# Revit family: MAXXflo EVO CWH 150-302
name_source: partatom
category: Generic Models
units: mm (PartAtom-declared; Revit-internal decimal feet)

## family parameters
Always vertical = Yes
Can host rebar = No
Cut with Voids When Loaded = No
Part Type = Normal
Room Calculation Point = No
Round Connector Dimension = Use Diameter
Shared = No
Work Plane-Based = No

## types (1)
- Standard
    6 Monthly = 0
    Access Clearance Bottom = 0 mm  [stored 0 ft]
    Access Clearance Front = 800 mm  [stored 2.62467 ft]
    Access Clearance Left = 300 mm
    Access Clearance Rear = 20 mm  [stored 0.0656168 ft]
    Access Clearance Right = 25 mm  [stored 0.082021 ft]
    Access Clearance Top = 400 mm  [stored 1.31234 ft]
    Air Inlet Connection Size = 200 mm  [stored 0.656168 ft]
    Annually = 32-12, 32.13, 32-10,
    BMS Links = Yes
    Bespoke Timeframe = 0
    CE Approval = 0558DL2312
    Clean Out Cover and Inspection Opening Size = 0 mm  [stored 0 ft]
    Colour = Cover = White (RAL 9016), Tower = Anthracite Grey (RAL 7016), Base = Dark Grey (RAL 7021)
    Condensate Drain Connection Type = Other
    Condensate Drain Size = 41 mm  [stored 0.134514 ft]
    Connector_1_Diameter = 45 mm
    Connector_2_Diameter = 30 mm  [stored 0.0984252 ft]
    Connector_3_Diameter = 45 mm
    Connector_4_Diameter = 30 mm  [stored 0.0984252 ft]
    Connector_5_Diameter = 28 mm  [stored 0.0918635 ft]
    Connector_6_Diameter = 28 mm  [stored 0.0918635 ft]
    Connector_7_Diameter = 41 mm  [stored 0.134514 ft]
    Connector_8_Diameter = 200 mm  [stored 0.656168 ft]
    Continuous output at 44 degree differential = 0.81000 L/s
    Continuous output at 50 degree differential = 0.71000 L/s
    Control Options = On/off
    Control Thermostat Range = 5-65ºC
    Control Type = Internal
    Daily = 0
    Default Elevation = 0 mm  [stored 0 ft]
    Description = BIM Model MAXXflo EVO CWH150/302
    Drain Connection Size = 22 mm  [stored 0.0721785 ft]
    Drain Connection Type = Other
    Embodied Carbon = 0
    Energy Technology List = 0
    Environmental Product Declaration = 0
    ErP Energy Label = A
    Expected Life = 10
    External Material = Steel
    Features = High efficiency condensing stainless steel; direct storage water heater
    Finish = Painted
    Flow and Return Connection Size = 38 mm
    Flow and Return Connection Type = Threaded
    Flue Connection size = 130 mm  [stored 0.426509 ft]
    Flue or Air Intake Classification = B23, C13, C33 C53, C63
    Frequency = 50 Hz
    Fuel Connection Size = 25 mm  [stored 0.082021 ft]
    Fuel Connection Type = Threaded
    Fuel Type = Gas - NG
    Full Load Current = 1.560 A
    Fuse Rating = 5.000 A
    Gas Consumption rate = 13.7 m3/h
    Green Guide for Specification = 0
    Gross Input = 149900 W
    Gross Weight = 539.00 kg
    Heat Exchanger Material = Stainless Steel
    Heat Generator Efficiency = 97
    Heat Generator Load Profile = XXL
    Heat Generator Thermal Efficiency = 98.2
    Heat up time = 7.2 mins
    Heater Operation = Fully condensing
    IK Rating = 0
    IP Rating = IP20
    Insulation Thickness = 50 mm  [stored 0.164042 ft]
    Insulation Type = NEOPOR
    Interlocks = Yes
    LPG Consumption rate = 5.6 m3/h
    Life Cycle Analysis = 0
    Location of Manufacturer = 0
    Maintenance Required 0 to 300hrs = 0
    Maintenance Required 1001 to 2000hrs = 0
    Maintenance Required 2001 to 4000hrs = 0
    Maintenance Required 301 to 600hrs = 0
    Maintenance Required 4001 to 8000hrs = 0
    Maintenance Required 601 to 1000hrs = 0
    Maintenance Required 8001 to 12000hrs = 0
    Manufacturer = Andrews Water Heaters
    Manufacturer Website = https://www.andrewswaterheaters.co.uk
    Material Ingredient Reporting = 0
    Maximum Gas Inlet Pressure = 0.0 bar
    Maximum LPG Inlet Pressure = 0.1 bar
    Maximum Oil Inlet Pressure = 0.0 bar
    Maximum Operating Pressure when Open Vented = 9.0 bar
    Maximum Operating Pressure when Unvented = 8.0 bar
    Maximum Power Consumption = 359 W
    Maximum Water Temperature = 70
    Minimum Gas Inlet Pressure = 0.0 bar
    Minimum LPG Inlet Pressure = 0.0 bar
    Minimum Oil Inlet Pressure = 0.0 bar
    Minimum Operating Pressure = 0.8 bar
    Minimum Power Consumption = 6 W
    Model = MAXXflo EVO CWH150/302
    Monthly = 0
    Mounting = Floor Standing
    NOx Emissions = 36
    Nominal Gas Inlet Pressure = 0.0 bar
    Nominal LPG Inlet Pressure = 0.0 bar
    Nominal Oil Inlet Pressure = 0.0 bar
    O&M Manual = https://www.andrewswaterheaters.co.uk
    Oil Consumption rate = 0
    Overall Height = 2008 mm  [stored 6.58793 ft]
    Overall Length = 1154 mm  [stored 3.78609 ft]
    Overall Width = 671 mm  [stored 2.20144 ft]
    Product Literature = https://www.andrewswaterheaters.co.uk
    Product Model Number = CWH 150/302
    Product Range = MAXXflo EVO
    Quarterly = 32-12,
    Recovery Rate = 0.71000 L/s
    Reference Standard = BS EN 89:2015
    Responsible Extraction of Materials = 0
    Responsible Sourcing of Materials = 0
    Safety Valve Connection Size = 28 mm  [stored 0.0918635 ft]
    Safety Valve Connection Type = Other
    Secondary Return Connection Size = 25 mm  [stored 0.082021 ft]
    Secondary Return Connection Type = Threaded
    Shape = Rectangular (Vertical)
    Shipping Weight = 296.00 kg
    Sound Pressure Level = 66 dBA
    Standby Current = 0.024 A
    Standing Loss = 94 W
    Starting Current = 0.000 A
    Supply Phase = 1
    Type = Direct fired hot water generation
    Voltage = 230 V
    WRAS Approval = Reg4 in progress
    Warranty ID = 0
    Water Content = 300 m³
    Water Treatment Required = Yes
    Weekly = 0

note: [stored X ft] marks values corroborated as IEEE doubles in the binary element streams (Revit-internal decimal feet)

## geometry (parser evidence)
native form markers: Sweep x3
no freeform markers — native parametric forms only
